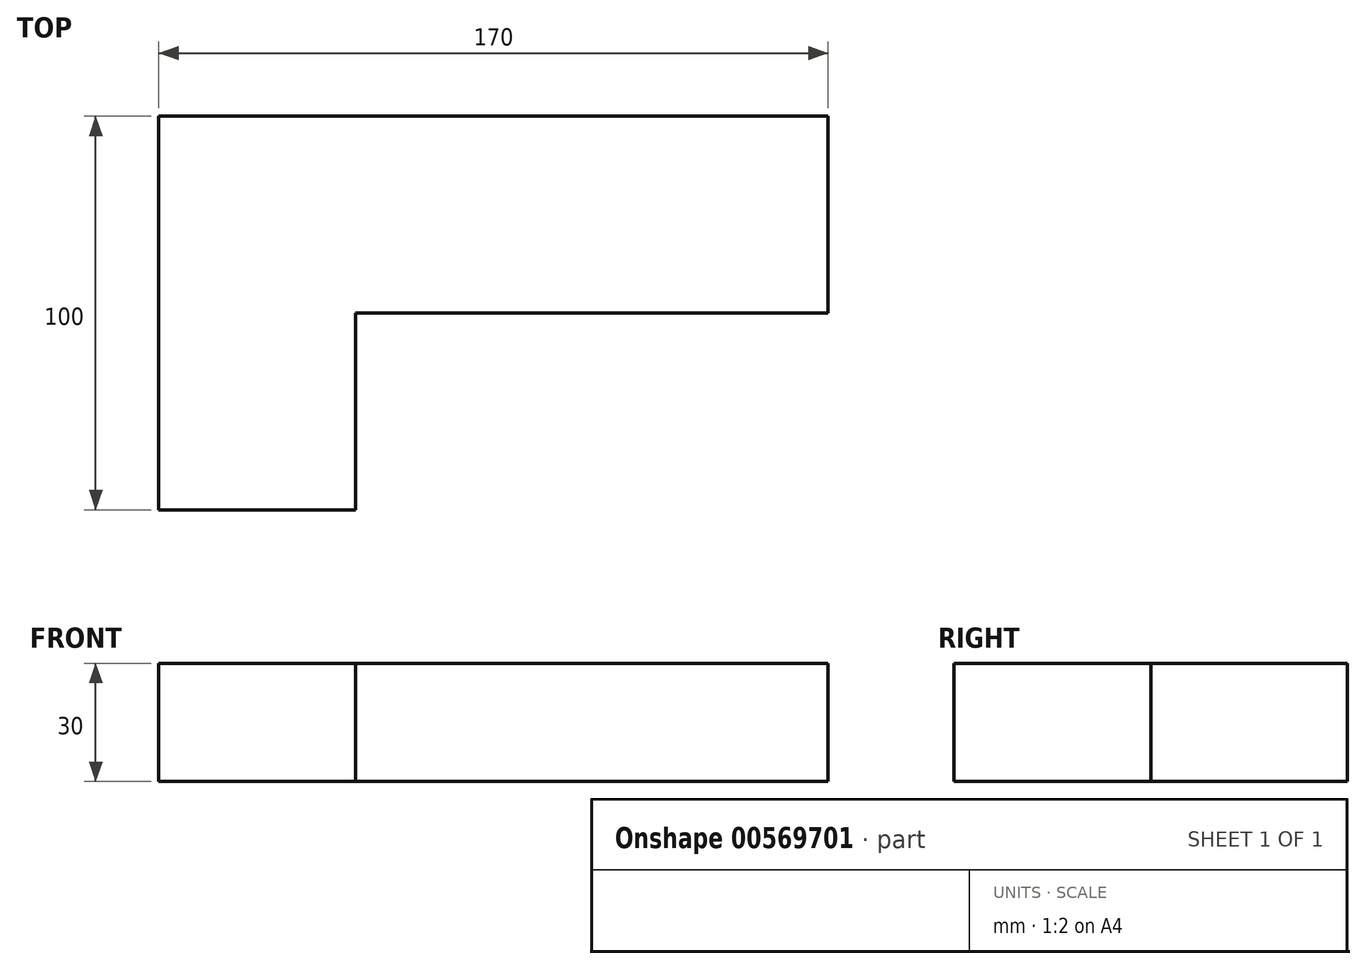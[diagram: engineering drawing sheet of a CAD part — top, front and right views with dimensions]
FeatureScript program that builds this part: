
annotation { "Feature Type Name" : "Feature", "Feature Type Description" : "" }
export const myFeature = defineFeature(function(context is Context, id is Id, definition is map)
    precondition{}
    {
        {
            var Q0;
            Q0=qCreatedBy(makeId("Top.planeOp"),FACE);
            var sketch = newSketch(context, id + "F0", { "sketchPlane" : qUnion([Q0])});
            skLineSegment(sketch, "E0", {"start": v(-85, 50) * mm, "end": v(-85, -50) * mm});
            skLineSegment(sketch, "E1", {"start": v(-85, -50) * mm, "end": v(-35, -50) * mm});
            skLineSegment(sketch, "E2", {"start": v(-35, -50) * mm, "end": v(-35, 0) * mm});
            skLineSegment(sketch, "E3", {"start": v(-35, 0) * mm, "end": v(85, 0) * mm});
            skLineSegment(sketch, "E4", {"start": v(85, 0) * mm, "end": v(85, 50) * mm});
            skLineSegment(sketch, "E5", {"start": v(85, 50) * mm, "end": v(-85, 50) * mm});
            skSolve(sketch);
        }
        {
            var Q0;
            Q0 = qSketchRegion(id + "F0", true);
            extrude(context, id + "F1", {"entities" : qUnion([Q0]), "depth" : 30 * mm, "offsetDistance" : 25 * mm});
        }
    });
